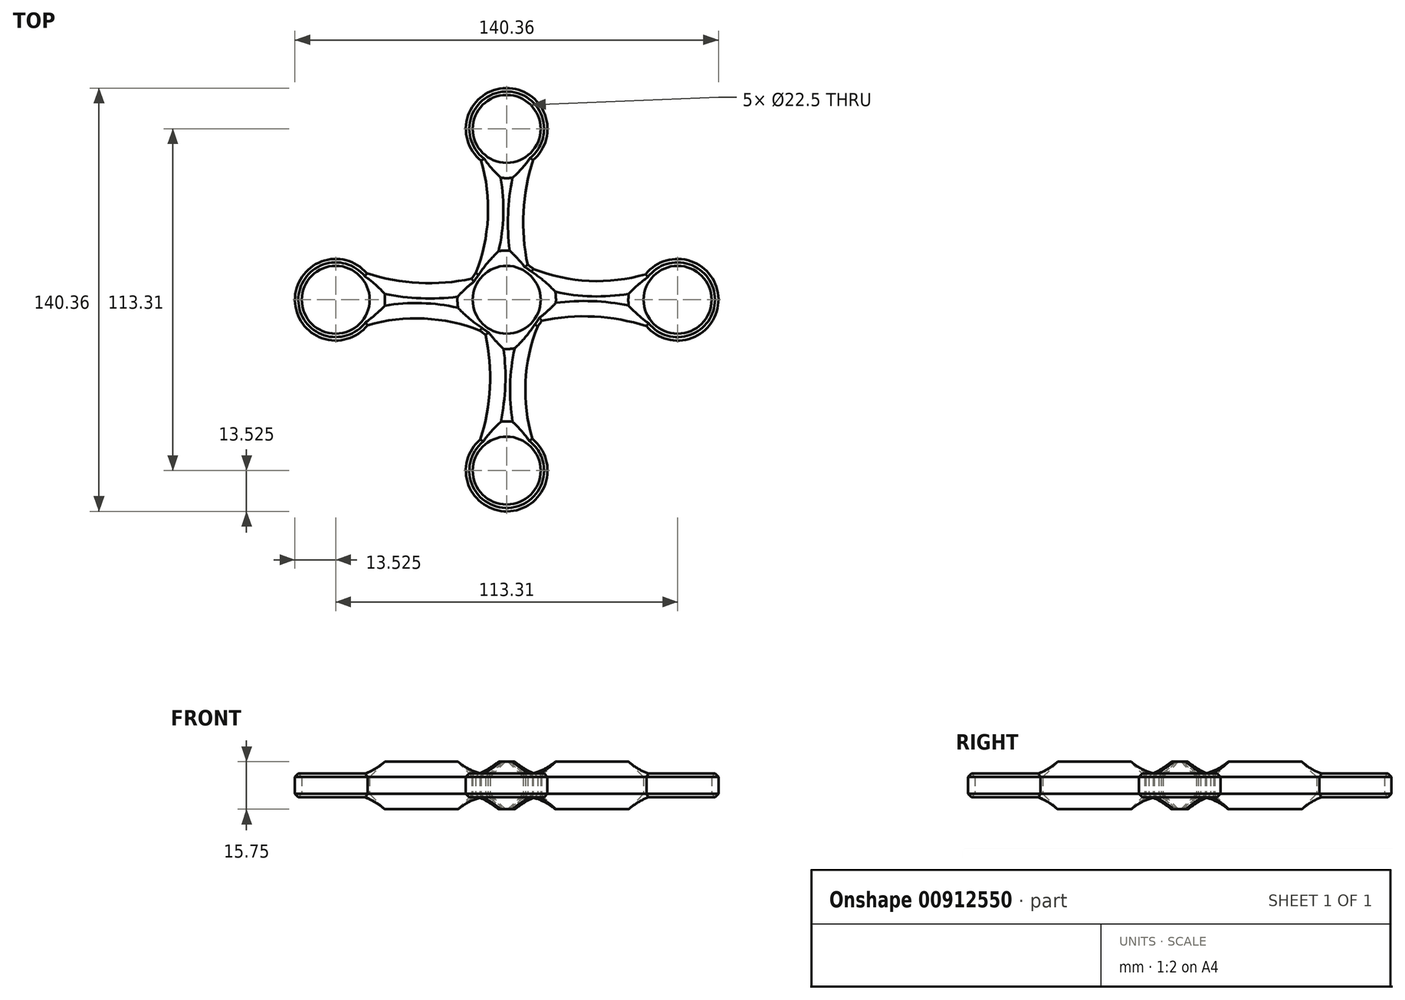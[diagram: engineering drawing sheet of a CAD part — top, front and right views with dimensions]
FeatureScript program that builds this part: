
annotation { "Feature Type Name" : "Feature", "Feature Type Description" : "" }
export const myFeature = defineFeature(function(context is Context, id is Id, definition is map)
    precondition{}
    {
        {
            var Q0;
            Q0=qCreatedBy(makeId("Top.planeOp"),FACE);
            var sketch = newSketch(context, id + "F0", { "sketchPlane" : qUnion([Q0])});
            skCircle(sketch, "E0", {"center": v(0, 0) * mm, "radius": 11.25 * mm});
            skCircle(sketch, "E1", {"center": v(0, 56.66) * mm, "radius": 11.25 * mm});
            skArc(sketch, "E2", {"start": v(8.74, 46.33) * mm, "mid": v(-0.18, 70.18) * mm, "end": v(-8.47, 46.1) * mm});
            skArc(sketch, "E3", {"start": v(-10.25, 8.83) * mm, "mid": v(2.15, -13.35) * mm, "end": v(6.95, 11.6) * mm});
            skArc(sketch, "E4", {"start": v(-10.25, 8.83) * mm, "mid": v(-6.24, 27.32) * mm, "end": v(-8.47, 46.1) * mm});
            skArc(sketch, "E5", {"start": v(8.74, 46.33) * mm, "mid": v(5.58, 29.08) * mm, "end": v(6.95, 11.6) * mm});
            skArc(sketch, "E6.1.0", {"start": v(-46.33, 8.74) * mm, "mid": v(-70.18, -0.18) * mm, "end": v(-46.1, -8.47) * mm});
            skCircle(sketch, "E6.1.1", {"center": v(-56.66, 0) * mm, "radius": 11.25 * mm});
            skArc(sketch, "E6.1.2", {"start": v(-8.83, -10.25) * mm, "mid": v(-27.32, -6.24) * mm, "end": v(-46.1, -8.47) * mm});
            skArc(sketch, "E6.1.3", {"start": v(-46.33, 8.74) * mm, "mid": v(-29.08, 5.58) * mm, "end": v(-11.6, 6.95) * mm});
            skArc(sketch, "E6.2.0", {"start": v(-8.74, -46.33) * mm, "mid": v(0.18, -70.18) * mm, "end": v(8.47, -46.1) * mm});
            skCircle(sketch, "E6.2.1", {"center": v(0, -56.66) * mm, "radius": 11.25 * mm});
            skArc(sketch, "E6.2.2", {"start": v(10.25, -8.83) * mm, "mid": v(6.24, -27.32) * mm, "end": v(8.47, -46.1) * mm});
            skArc(sketch, "E6.2.3", {"start": v(-8.74, -46.33) * mm, "mid": v(-5.58, -29.08) * mm, "end": v(-6.95, -11.6) * mm});
            skArc(sketch, "E6.3.0", {"start": v(46.33, -8.74) * mm, "mid": v(70.18, 0.18) * mm, "end": v(46.1, 8.47) * mm});
            skCircle(sketch, "E6.3.1", {"center": v(56.66, 0) * mm, "radius": 11.25 * mm});
            skArc(sketch, "E6.3.2", {"start": v(8.83, 10.25) * mm, "mid": v(27.32, 6.24) * mm, "end": v(46.1, 8.47) * mm});
            skArc(sketch, "E6.3.3", {"start": v(46.33, -8.74) * mm, "mid": v(29.08, -5.58) * mm, "end": v(11.6, -6.95) * mm});
            skSolve(sketch);
        }
        {
            var Q0;
            Q0=makeQuery(id+"F0.imprint","IMPRINT",FACE,{"disambiguationData":[TD([[makeQuery(id+"F0.imprint","IMPRINT",EDGE,{"derivedFrom":sQuery(id+"F0.wireOp",EDGE,"E6.1.0")}),1.0]])]});
            var Q1;
            Q1=makeQuery(id+"F0.imprint","IMPRINT",FACE,{"disambiguationData":[TD([[makeQuery(id+"F0.imprint","IMPRINT",EDGE,{"derivedFrom":sQuery(id+"F0.wireOp",EDGE,"E0")}),-1.0]])]});
            var Q2;
            Q2=makeQuery(id+"F0.imprint","IMPRINT",FACE,{"disambiguationData":[TD([[makeQuery(id+"F0.imprint","IMPRINT",EDGE,{"derivedFrom":sQuery(id+"F0.wireOp",EDGE,"E6.3.0")}),1.0]])]});
            var Q3;
            Q3=makeQuery(id+"F0.imprint","IMPRINT",FACE,{"disambiguationData":[TD([[makeQuery(id+"F0.imprint","IMPRINT",EDGE,{"derivedFrom":sQuery(id+"F0.wireOp",EDGE,"E6.2.0")}),1.0]])]});
            extrude(context, id + "F1", {"entities" : qUnion([Q0, Q1, Q2, Q3]), "depth" : 15.75 * mm, "offsetDistance" : 25.4 * mm});
        }
        {
            var Q0;
            Q0=makeQuery(id+"F1.opExtrude","CAP_FACE",FACE,{"disambiguationData":[OSD([sQuery(id+"F0.wireOp",EDGE,"E0"),sQuery(id+"F0.wireOp",EDGE,"E1"),sQuery(id+"F0.wireOp",EDGE,"E2"),sQuery(id+"F0.wireOp",EDGE,"E3"),sQuery(id+"F0.wireOp",EDGE,"E4"),sQuery(id+"F0.wireOp",EDGE,"E5"),sQuery(id+"F0.wireOp",EDGE,"E6.1.0"),sQuery(id+"F0.wireOp",EDGE,"E6.1.1"),sQuery(id+"F0.wireOp",EDGE,"E6.1.2"),sQuery(id+"F0.wireOp",EDGE,"E6.1.3"),sQuery(id+"F0.wireOp",EDGE,"E6.2.0"),sQuery(id+"F0.wireOp",EDGE,"E6.2.1"),sQuery(id+"F0.wireOp",EDGE,"E6.2.2"),sQuery(id+"F0.wireOp",EDGE,"E6.2.3"),sQuery(id+"F0.wireOp",EDGE,"E6.3.0"),sQuery(id+"F0.wireOp",EDGE,"E6.3.1"),sQuery(id+"F0.wireOp",EDGE,"E6.3.2"),sQuery(id+"F0.wireOp",EDGE,"E6.3.3")])],"isStart":false});
            chamfer(context, id + "F2", {"entities" : qUnion([Q0]), "width" : 5.08 * mm, "tangentPropagation" : true});
        }
        {
            var Q0;
            Q0=makeQuery(id+"F1.opExtrude","CAP_FACE",FACE,{"disambiguationData":[OSD([sQuery(id+"F0.wireOp",EDGE,"E0"),sQuery(id+"F0.wireOp",EDGE,"E1"),sQuery(id+"F0.wireOp",EDGE,"E2"),sQuery(id+"F0.wireOp",EDGE,"E3"),sQuery(id+"F0.wireOp",EDGE,"E4"),sQuery(id+"F0.wireOp",EDGE,"E5"),sQuery(id+"F0.wireOp",EDGE,"E6.1.0"),sQuery(id+"F0.wireOp",EDGE,"E6.1.1"),sQuery(id+"F0.wireOp",EDGE,"E6.1.2"),sQuery(id+"F0.wireOp",EDGE,"E6.1.3"),sQuery(id+"F0.wireOp",EDGE,"E6.2.0"),sQuery(id+"F0.wireOp",EDGE,"E6.2.1"),sQuery(id+"F0.wireOp",EDGE,"E6.2.2"),sQuery(id+"F0.wireOp",EDGE,"E6.2.3"),sQuery(id+"F0.wireOp",EDGE,"E6.3.0"),sQuery(id+"F0.wireOp",EDGE,"E6.3.1"),sQuery(id+"F0.wireOp",EDGE,"E6.3.2"),sQuery(id+"F0.wireOp",EDGE,"E6.3.3")])],"isStart":true});
            chamfer(context, id + "F3", {"entities" : qUnion([Q0]), "width" : 5.08 * mm, "tangentPropagation" : true});
        }
    });
